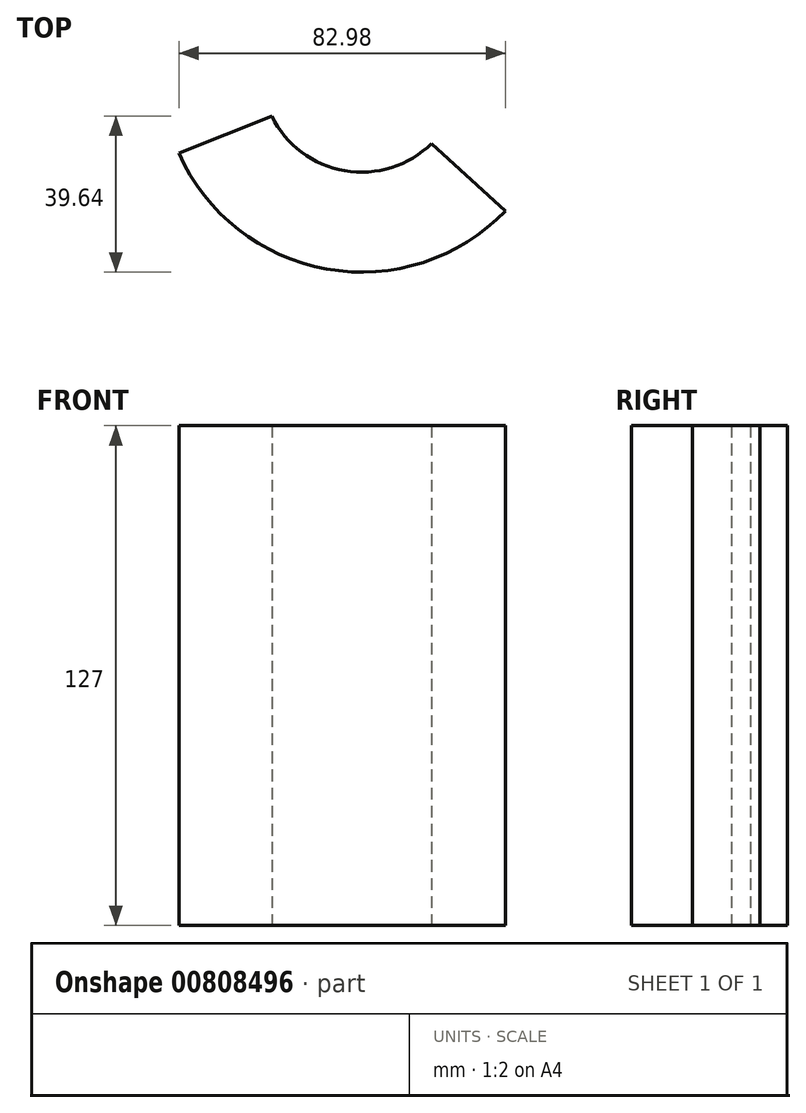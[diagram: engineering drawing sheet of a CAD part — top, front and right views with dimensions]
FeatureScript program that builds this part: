
annotation { "Feature Type Name" : "Feature", "Feature Type Description" : "" }
export const myFeature = defineFeature(function(context is Context, id is Id, definition is map)
    precondition{}
    {
        {
            var Q0;
            Q0=qCreatedBy(makeId("Top.planeOp"),FACE);
            var sketch = newSketch(context, id + "F0", { "sketchPlane" : qUnion([Q0])});
            skArc(sketch, "E0", {"start": v(-46.45, -20.58) * mm, "mid": v(-8.87, -50.02) * mm, "end": v(36.53, -35.3) * mm});
            skArc(sketch, "E1", {"start": v(-22.82, -11.16) * mm, "mid": v(-4.29, -25.04) * mm, "end": v(17.8, -18.12) * mm});
            skLineSegment(sketch, "E2", {"start": v(17.8, -18.12) * mm, "end": v(36.53, -35.3) * mm});
            skLineSegment(sketch, "E3", {"start": v(-22.82, -11.16) * mm, "end": v(-46.45, -20.58) * mm});
            skSolve(sketch);
        }
        {
            var Q0;
            Q0=makeQuery(id+"F0.imprint","IMPRINT",FACE,{"disambiguationData":[TD([[makeQuery(id+"F0.imprint","IMPRINT",EDGE,{"derivedFrom":sQuery(id+"F0.wireOp",EDGE,"E0")}),1.0]])]});
            extrude(context, id + "F1", {"entities" : qUnion([Q0]), "depth" : 127 * mm, "offsetDistance" : 25.4 * mm});
        }
    });
